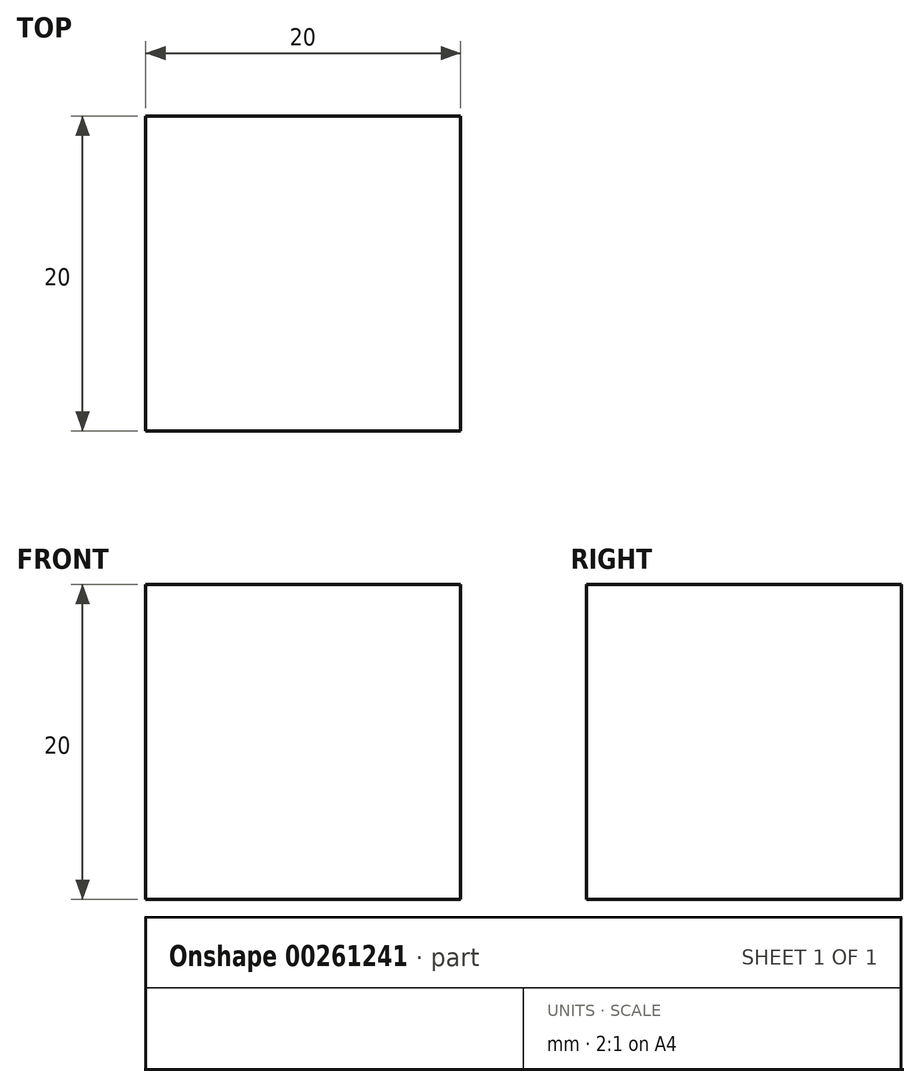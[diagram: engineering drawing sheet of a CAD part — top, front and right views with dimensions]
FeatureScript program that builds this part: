
annotation { "Feature Type Name" : "Feature", "Feature Type Description" : "" }
export const myFeature = defineFeature(function(context is Context, id is Id, definition is map)
    precondition{}
    {
        {
            var Q0;
            Q0=qCreatedBy(makeId("Top.planeOp"),FACE);
            var sketch = newSketch(context, id + "F0", { "sketchPlane" : qUnion([Q0])});
            skLineSegment(sketch, "E0.bottom", {"start": v(-7.77, 9.04) * mm, "end": v(12.23, 9.04) * mm});
            skLineSegment(sketch, "E0.top", {"start": v(-7.77, -10.96) * mm, "end": v(12.23, -10.96) * mm});
            skLineSegment(sketch, "E0.left", {"start": v(-7.77, 9.04) * mm, "end": v(-7.77, -10.96) * mm});
            skLineSegment(sketch, "E0.right", {"start": v(12.23, 9.04) * mm, "end": v(12.23, -10.96) * mm});
            skSolve(sketch);
        }
        {
            var Q0;
            Q0=makeQuery(id+"F0.imprint","IMPRINT",FACE,{"disambiguationData":[TD([[makeQuery(id+"F0.imprint","IMPRINT",EDGE,{"derivedFrom":sQuery(id+"F0.wireOp",EDGE,"E0.bottom")}),-1.0]])]});
            extrude(context, id + "F1", {"entities" : qUnion([Q0]), "depth" : 20 * mm});
        }
    });
